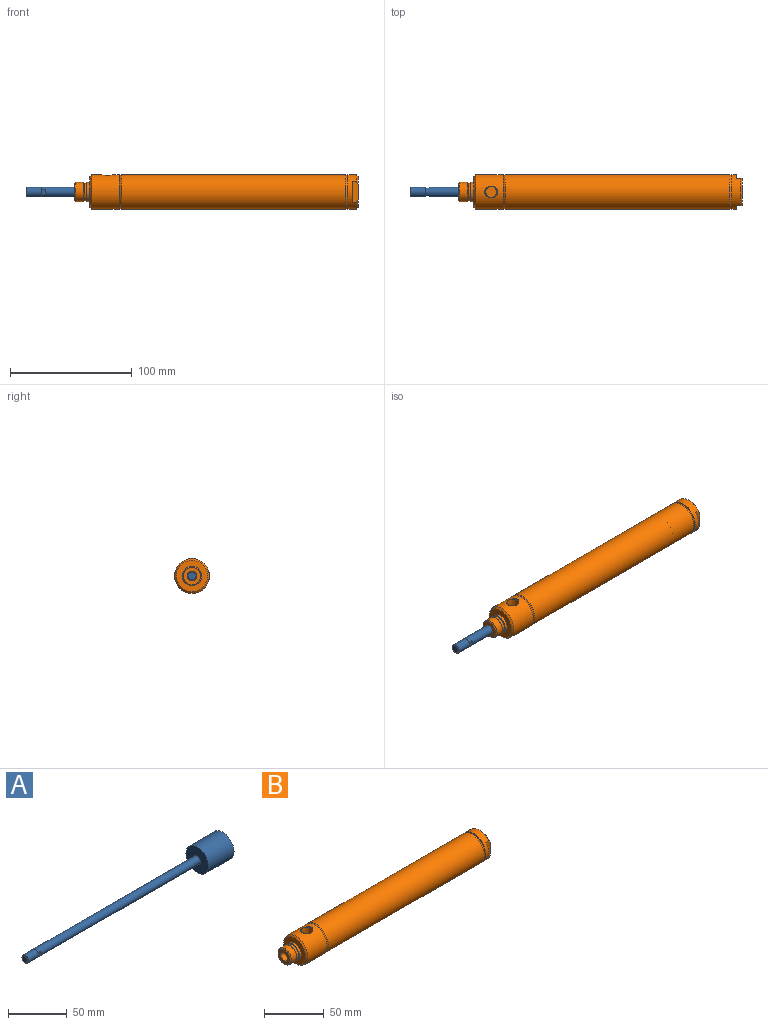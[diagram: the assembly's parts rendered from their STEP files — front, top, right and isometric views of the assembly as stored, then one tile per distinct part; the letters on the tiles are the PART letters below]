
ASSEMBLY  parts=2 mates=1
PART A: 15 faces, bbox 239.3x27x27 mm
  f0: plane 6.35x1.59mm, normal (-1,0,0), area 0mm2, adj f3,f5,f9,f12
  f1: plane 6.68x6.68mm, normal (-1,0,0), area 35mm2, adj f2
  f2: cone r=3.34mm half-angle=45deg, axis (1,0,0), area 20.5mm2, adj f1,f3
  f3: cylinder r=3.97mm len=12.07mm, axis (1,0,0), area 301mm2, adj f0,f2,f4,f10,f13
  f4: plane 6.35x1.59mm, normal (-1,0,0), area 0mm2, adj f3,f5,f9,f12
  f5: cylinder r=3.98mm len=195.59mm, axis (1,0,0), area 4852.6mm2, adj f0,f4,f6,f9,f11,f12,f14
  f6: plane 26.99x26.99mm, normal (-1,0,0), area 522.4mm2, adj f5,f7
  f7: cylinder r=13.49mm len=31.04mm, axis (1,0,0), area 2631.6mm2, adj f6,f8
  f8: plane 26.99x26.99mm, normal (1,0,0), area 572mm2, adj f7
  f9: plane 4.78x3.18mm, normal (0,1,0), area 15.2mm2, adj f0,f4,f5,f10,f11
  f10: plane 4.76x0.79mm, normal (1,0,0), area 2.6mm2, adj f3,f9
  f11: plane 4.78x0.8mm, normal (-1,0,0), area 2.6mm2, adj f5,f9
  f12: plane 4.78x3.18mm, normal (0,-1,0), area 15.2mm2, adj f0,f4,f5,f13,f14
  f13: plane 4.76x0.79mm, normal (1,0,0), area 2.6mm2, adj f3,f12
  f14: plane 4.78x0.8mm, normal (-1,0,0), area 2.6mm2, adj f5,f12
PART B: 36 faces, bbox 233.4x28.6x28.6 mm
  f0: cylinder r=14.29mm len=28.58mm, axis (1,0,0), area 482.8mm2, adj f1,f2,f18,f23,f24,f25,f26
  f1: cone r=14.29mm half-angle=45deg, axis (-1,0,0), area 52.7mm2, adj f0,f3,f23,f26
  f2: cone r=14.29mm half-angle=45deg, axis (-1,0,0), area 52.7mm2, adj f0,f3,f23,f26
  f3: plane 25.72x22.23mm, normal (1,0,0), area 395.4mm2, adj f1,f2,f23,f26,f29
  f4: cylinder r=14.29mm len=28.58mm, axis (1,0,0), area 1951.4mm2, adj f13,f14,f19,f20,f21
  f5: plane 14.2x14.2mm, normal (-1,0,0), area 108.6mm2, adj f6,f30
  f6: cone r=7.1mm half-angle=45deg, axis (1,0,0), area 56.1mm2, adj f5,f7
  f7: cylinder r=7.94mm len=15.88mm, axis (1,0,0), area 311.5mm2, adj f6,f8
  f8: cone r=7.94mm half-angle=45deg, axis (-1,0,0), area 56.1mm2, adj f7,f9
  f9: cylinder r=7.1mm len=14.2mm, axis (1,0,0), area 106.5mm2, adj f8,f10
  f10: plane 15.85x15.85mm, normal (-1,0,0), area 39mm2, adj f9,f11
  f11: cylinder r=7.92mm len=15.85mm, axis (1,0,0), area 118.9mm2, adj f10,f12
  f12: plane 25.72x25.72mm, normal (-1,0,0), area 322.2mm2, adj f11,f13
  f13: cone r=12.86mm half-angle=45deg, axis (1,0,0), area 172.3mm2, adj f4,f12
  f14: plane 28.58x28.58mm, normal (1,0,0), area 90.1mm2, adj f4,f15
  f15: cone r=13.25mm half-angle=30deg, axis (1,0,0), area 164.4mm2, adj f14,f16
  f16: cylinder r=14.2mm len=185.03mm, axis (1,0,0), area 16506.6mm2, adj f15,f17
  f17: cone r=14.2mm half-angle=30deg, axis (-1,0,0), area 164.4mm2, adj f16,f18
  f18: plane 28.58x28.58mm, normal (-1,0,0), area 90.1mm2, adj f0,f17
  f19: cone r=5.45mm half-angle=45deg, axis (0,0,1), area 5.6mm2, adj f4,f21
  f20: cone r=5.45mm half-angle=45deg, axis (0,0,1), area 5.6mm2, adj f4,f21
  f21: cone r=4.82mm half-angle=1.8deg, axis (0,0,1), area 272.9mm2, adj f4,f19,f20,f22
  f22: plane 9.06x9.06mm, normal (0,0,1), area 64.4mm2, adj f21
  f23: plane 17.96x4.78mm, normal (0,1,0), area 82.3mm2, adj f0,f1,f2,f3,f24
  f24: plane 17.96x3.18mm, normal (1,0,0), area 39mm2, adj f0,f23
  f25: plane 17.96x3.18mm, normal (1,0,0), area 39mm2, adj f0,f26
  f26: plane 17.96x4.78mm, normal (0,-1,0), area 82.3mm2, adj f0,f1,f2,f3,f25
  f27: plane 9.29x9.29mm, normal (1,0,0), area 67.8mm2, adj f28
  f28: cone r=4.65mm half-angle=1.8deg, axis (1,0,0), area 165.8mm2, adj f27,f29
  f29: cone r=4.82mm half-angle=45deg, axis (1,0,0), area 29mm2, adj f3,f28
  f30: cylinder r=3.98mm len=38.43mm, axis (1,0,0), area 959.8mm2, adj f5,f31
  f31: plane 26.99x26.99mm, normal (1,0,0), area 522.4mm2, adj f30,f32
  f32: cylinder r=13.49mm len=185.03mm, axis (1,0,0), area 15687.2mm2, adj f31,f33
  f33: plane 26.99x26.99mm, normal (-1,0,0), area 522.4mm2, adj f32,f34
  f34: cylinder r=3.98mm len=7.95mm, axis (1,0,0), area 41.2mm2, adj f33,f35
  f35: plane 7.95x7.95mm, normal (-1,0,0), area 49.6mm2, adj f34
PLACE A rot(axis=(-1,0,0),0deg) t=(-22.53,31.95,13.89)mm
PLACE B t=(1.43,31.95,13.89)mm
MATE slider A.f2 <-> B.f0  axis (1,0,0) through (200.92,31.95,13.89)mm
